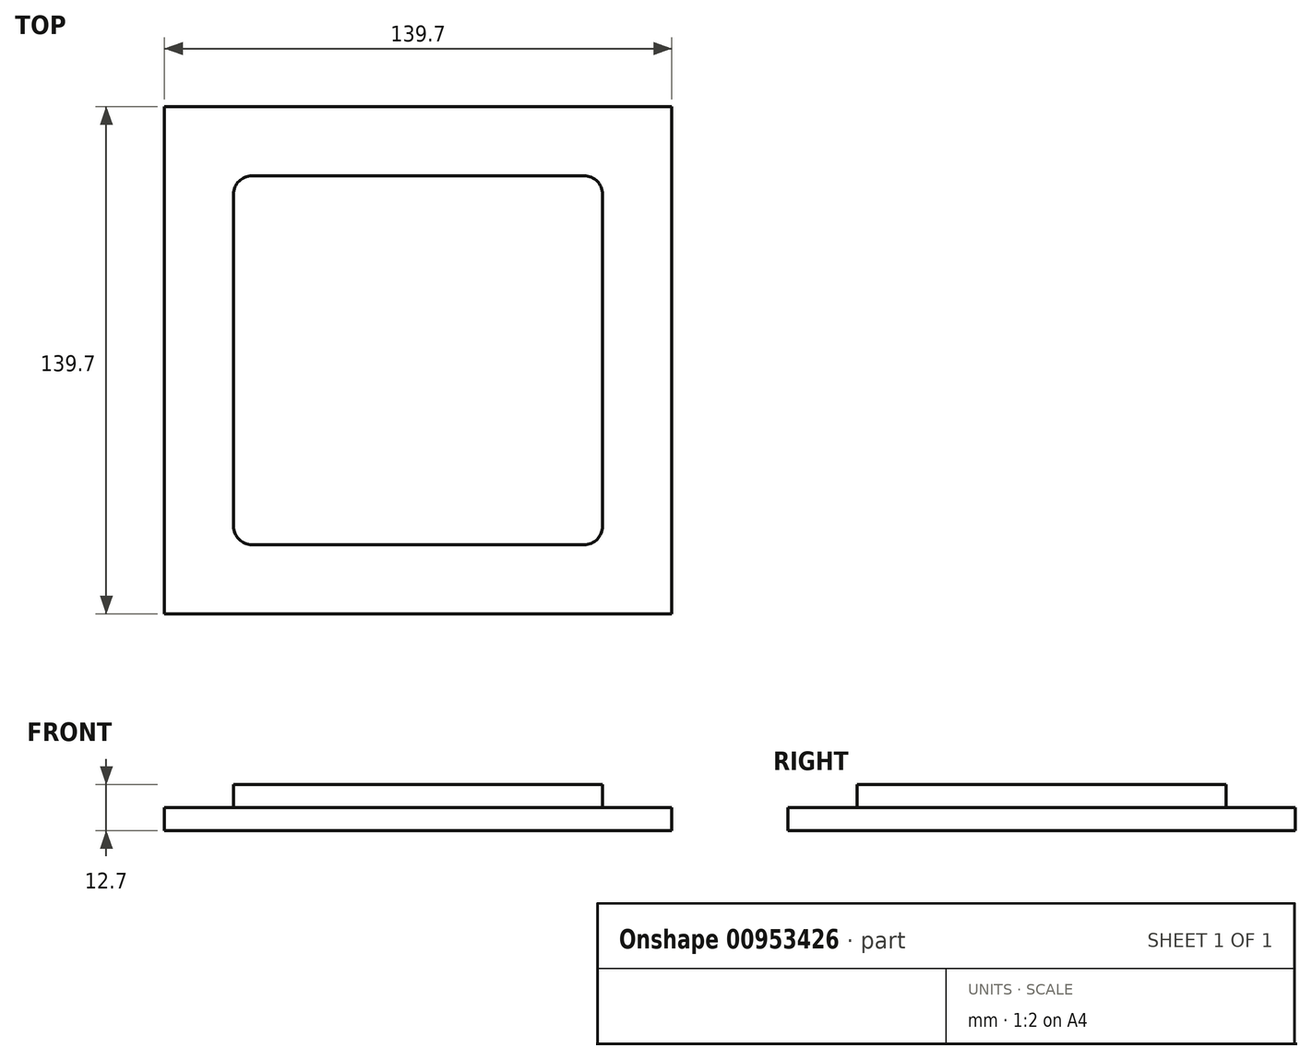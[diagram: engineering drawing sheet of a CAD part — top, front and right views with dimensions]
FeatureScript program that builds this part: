
annotation { "Feature Type Name" : "Feature", "Feature Type Description" : "" }
export const myFeature = defineFeature(function(context is Context, id is Id, definition is map)
    precondition{}
    {
        {
            var Q0;
            Q0=qCreatedBy(makeId("Top.planeOp"),FACE);
            var sketch = newSketch(context, id + "F0", { "sketchPlane" : qUnion([Q0])});
            skLineSegment(sketch, "E0.bottom", {"start": v(-69.85, 69.85) * mm, "end": v(69.85, 69.85) * mm});
            skLineSegment(sketch, "E0.top", {"start": v(-69.85, -69.85) * mm, "end": v(69.85, -69.85) * mm});
            skLineSegment(sketch, "E0.left", {"start": v(-69.85, 69.85) * mm, "end": v(-69.85, -69.85) * mm});
            skLineSegment(sketch, "E0.right", {"start": v(69.85, 69.85) * mm, "end": v(69.85, -69.85) * mm});
            skPoint(sketch, "E0.middle", {"position": v(0, 0) * mm});
            skSolve(sketch);
        }
        {
            var Q0;
            Q0=makeQuery(id+"F0.imprint","IMPRINT",FACE,{"disambiguationData":[TD([[makeQuery(id+"F0.imprint","IMPRINT",EDGE,{"derivedFrom":sQuery(id+"F0.wireOp",EDGE,"E0.bottom")}),-1.0]])]});
            extrude(context, id + "F1", {"entities" : qUnion([Q0]), "depth" : 6.35 * mm, "offsetDistance" : 25.4 * mm});
        }
        {
            var Q0;
            Q0=makeQuery(id+"F1.opExtrude","CAP_FACE",FACE,{"disambiguationData":[OSD([sQuery(id+"F0.wireOp",EDGE,"E0.bottom"),sQuery(id+"F0.wireOp",EDGE,"E0.top"),sQuery(id+"F0.wireOp",EDGE,"E0.left"),sQuery(id+"F0.wireOp",EDGE,"E0.right")])],"isStart":false});
            var sketch = newSketch(context, id + "F2", { "sketchPlane" : qUnion([Q0])});
            skLineSegment(sketch, "E1.bottom", {"start": v(-50.8, 50.8) * mm, "end": v(50.8, 50.8) * mm});
            skLineSegment(sketch, "E1.top", {"start": v(-50.8, -50.8) * mm, "end": v(50.8, -50.8) * mm});
            skLineSegment(sketch, "E1.left", {"start": v(-50.8, 50.8) * mm, "end": v(-50.8, -50.8) * mm});
            skLineSegment(sketch, "E1.right", {"start": v(50.8, 50.8) * mm, "end": v(50.8, -50.8) * mm});
            skPoint(sketch, "E1.middle", {"position": v(0, 0) * mm});
            skSolve(sketch);
        }
        {
            var Q0;
            Q0=makeQuery(id+"F2.imprint","IMPRINT",FACE,{"disambiguationData":[TD([[makeQuery(id+"F2.imprint","IMPRINT",EDGE,{"derivedFrom":sQuery(id+"F2.wireOp",EDGE,"E1.bottom")}),-1.0]])]});
            extrude(context, id + "F3", {"entities" : qUnion([Q0]), "operationType" : NewBodyOperationType.ADD, "depth" : 6.35 * mm, "offsetDistance" : 25.4 * mm});
        }
        {
            var Q0;
            Q0=makeQuery(id+"F3.opExtrude","SWEPT_EDGE",EDGE,{"disambiguationData":[OSD([sQuery(id+"F2.wireOp",EDGE,"E1.top"),sQuery(id+"F2.wireOp",EDGE,"E1.right")])]});
            var Q1;
            Q1=makeQuery(id+"F3.opExtrude","SWEPT_EDGE",EDGE,{"disambiguationData":[OSD([sQuery(id+"F2.wireOp",EDGE,"E1.bottom"),sQuery(id+"F2.wireOp",EDGE,"E1.right")])]});
            var Q2;
            Q2=makeQuery(id+"F3.opExtrude","SWEPT_EDGE",EDGE,{"disambiguationData":[OSD([sQuery(id+"F2.wireOp",EDGE,"E1.top"),sQuery(id+"F2.wireOp",EDGE,"E1.left")])]});
            var Q3;
            Q3=makeQuery(id+"F3.opExtrude","SWEPT_EDGE",EDGE,{"disambiguationData":[OSD([sQuery(id+"F2.wireOp",EDGE,"E1.bottom"),sQuery(id+"F2.wireOp",EDGE,"E1.left")])]});
            fillet(context, id + "F4", {"entities" : qUnion([Q0, Q1, Q2, Q3]), "radius" : 5.08 * mm, "tangentPropagation" : true, "allowEdgeOverflow" : false});
        }
    });
